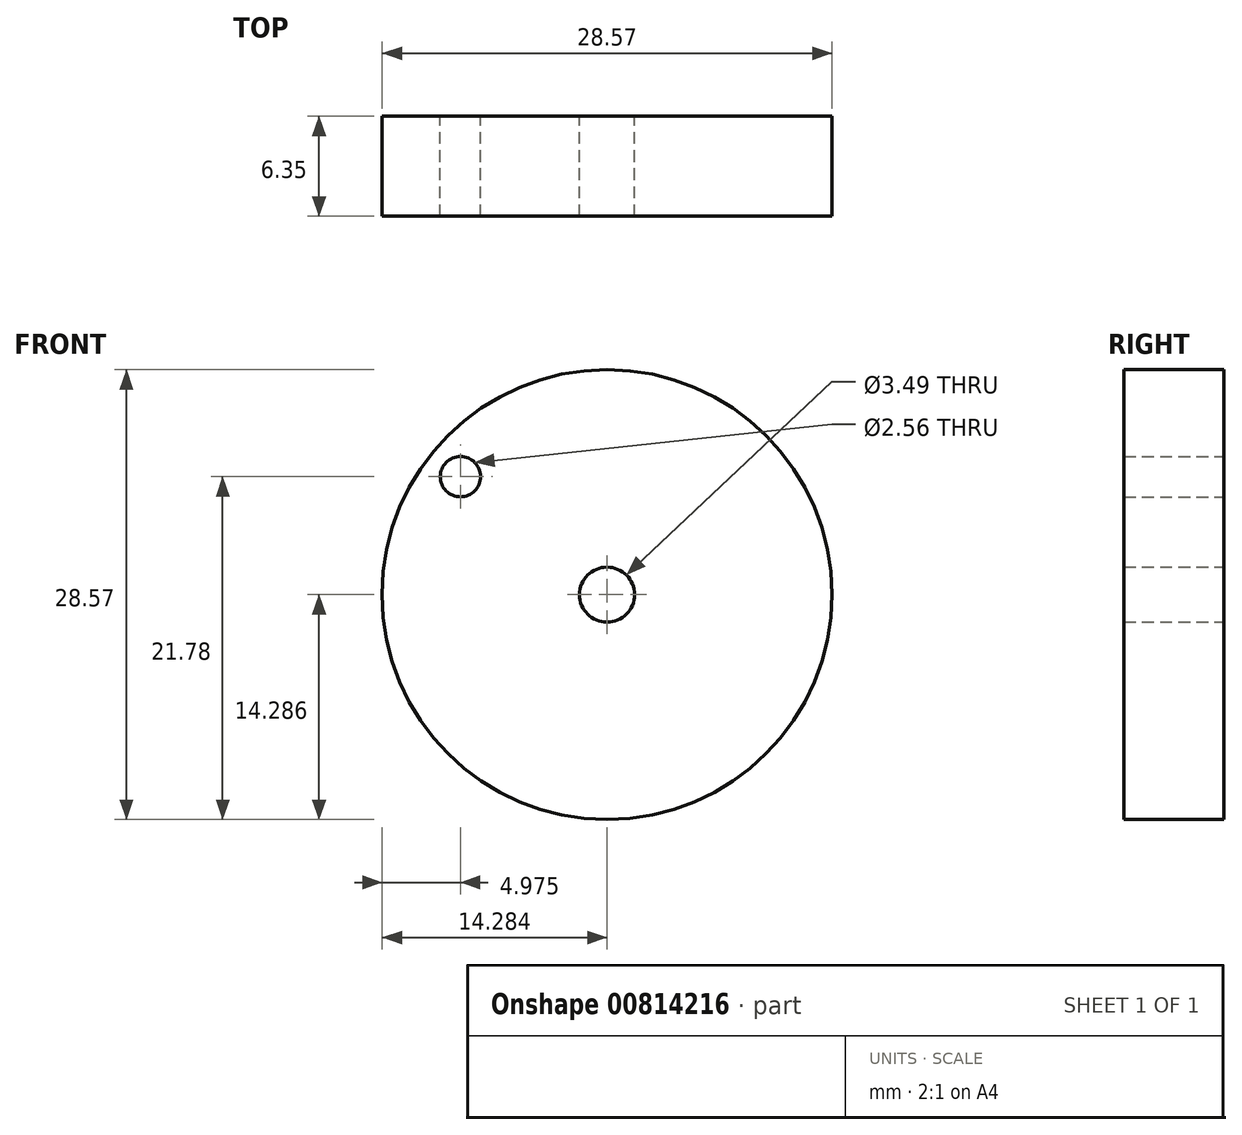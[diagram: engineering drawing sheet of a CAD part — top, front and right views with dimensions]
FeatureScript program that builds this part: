
annotation { "Feature Type Name" : "Feature", "Feature Type Description" : "" }
export const myFeature = defineFeature(function(context is Context, id is Id, definition is map)
    precondition{}
    {
        {
            var Q0;
            Q0=qCreatedBy(makeId("Front.planeOp"),FACE);
            var sketch = newSketch(context, id + "F0", { "sketchPlane" : qUnion([Q0])});
            skCircle(sketch, "E0", {"center": v(-50.18, 47.04) * mm, "radius": 14.29 * mm});
            skCircle(sketch, "E1", {"center": v(-50.18, 47.04) * mm, "radius": 1.75 * mm});
            skCircle(sketch, "E2", {"center": v(-59.48, 54.53) * mm, "radius": 1.28 * mm});
            skSolve(sketch);
        }
        {
            var Q0;
            Q0=makeQuery(id+"F0.imprint","IMPRINT",FACE,{"disambiguationData":[TD([[makeQuery(id+"F0.imprint","IMPRINT",EDGE,{"derivedFrom":sQuery(id+"F0.wireOp",EDGE,"E0")}),1.0]])]});
            extrude(context, id + "F1", {"entities" : qUnion([Q0]), "depth" : 6.35 * mm, "offsetDistance" : 25.4 * mm});
        }
    });
